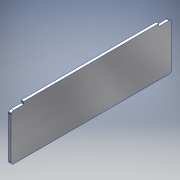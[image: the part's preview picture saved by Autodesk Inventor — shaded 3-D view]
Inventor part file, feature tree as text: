
AUTODESK INVENTOR PART (.ipt)
format: ipt  version: 2018.1 (Build 221171000, 171)  size: 124,416 bytes
history: native  units: in
note: dims shown in document units (in); Inventor stores cm internally (conversion verified against a paired STEP export)
features: sheet_metal_op x1, sketch x1, other x1
ambient origin geometry x8: Origin, YZ Plane, XZ Plane, XY Plane, X Axis, Y Axis, Z Axis, Center Point
bodies: Solid1 (feature_tree)
feature tree (3):
  sheet_metal_op  "Face1"
  sketch  "Sketch1"  dims[d0=0.125in]
  other  "Plate1"
